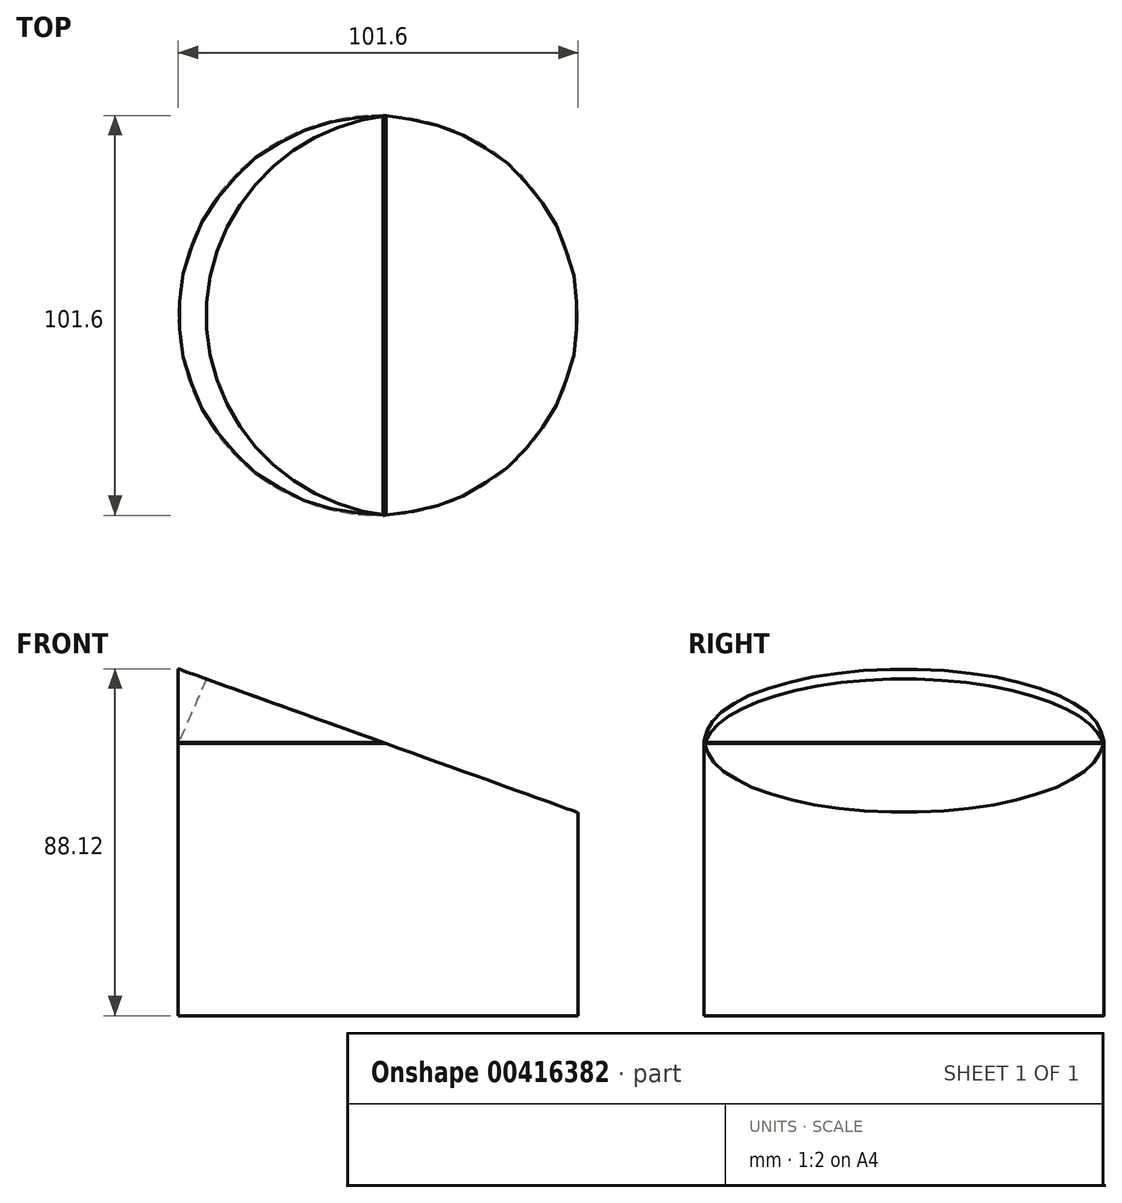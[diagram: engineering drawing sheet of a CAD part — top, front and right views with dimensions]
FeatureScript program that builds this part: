
annotation { "Feature Type Name" : "Feature", "Feature Type Description" : "" }
export const myFeature = defineFeature(function(context is Context, id is Id, definition is map)
    precondition{}
    {
        {
            var Q0;
            Q0=qCreatedBy(makeId("Front.planeOp"),FACE);
            var sketch = newSketch(context, id + "F0", { "sketchPlane" : qUnion([Q0])});
            skLineSegment(sketch, "E0", {"start": v(0, 0) * mm, "end": v(101.6, 0) * mm});
            skLineSegment(sketch, "E1", {"start": v(0, 0) * mm, "end": v(-101.6, 0) * mm});
            skFitSpline(sketch, "E2", {"points": [v(-101.6, 0) * mm, v(0, 152.4) * mm, v(101.6, 0) * mm], "startDerivative": vector(212.3, 35.26) * mm, "endDerivative": vector(256.16, -42) * mm});
            skLineSegment(sketch, "E3", {"start": v(0, 0) * mm, "end": v(0, 152.4) * mm});
            skSolve(sketch);
        }
        {
            var Q0;
            Q0=makeQuery(id+"F0.imprint","IMPRINT",FACE,{"disambiguationData":[TD([[makeQuery(id+"F0.imprint","IMPRINT",EDGE,{"derivedFrom":sQuery(id+"F0.wireOp",EDGE,"E0")}),1.0]])]});
            var Q1;
            Q1=sQuery(id+"F0.wireOp",EDGE,"E3");
            revolve(context, id + "F1", {"entities" : qUnion([Q0]), "axis" : qUnion([Q1]), "revolveType" : RevolveType.FULL});
        }
        {
            var Q0;
            Q0=qCreatedBy(makeId("Right.planeOp"),FACE);
            var sketch = newSketch(context, id + "F2", { "sketchPlane" : qUnion([Q0])});
            skLineSegment(sketch, "E4", {"start": v(0, 0) * mm, "end": v(0, 107.44) * mm});
            skSolve(sketch);
        }
        {
            var Q0;
            Q0=qCreatedBy(makeId("Front.planeOp"),FACE);
            var sketch = newSketch(context, id + "F3", { "sketchPlane" : qUnion([Q0])});
            skLineSegment(sketch, "E5", {"start": v(194.23, 0) * mm, "end": v(-165.07, 129.22) * mm});
            skPoint(sketch, "E6", {"position": v(0, 69.85) * mm});
            skLineSegment(sketch, "E7", {"start": v(-165.07, 129.22) * mm, "end": v(-130.7, 224.82) * mm});
            skLineSegment(sketch, "E8", {"start": v(194.23, 0) * mm, "end": v(228.61, 95.6) * mm});
            skLineSegment(sketch, "E9", {"start": v(-130.7, 224.82) * mm, "end": v(228.61, 95.6) * mm});
            skSolve(sketch);
        }
        {
            var Q0;
            Q0=qCreatedBy(makeId("Top.planeOp"),FACE);
            var sketch = newSketch(context, id + "F4", { "sketchPlane" : qUnion([Q0])});
            skCircle(sketch, "E10", {"center": v(0, 0) * mm, "radius": 50.8 * mm});
            skCircle(sketch, "E11", {"center": v(0, 0) * mm, "radius": 164.6 * mm});
            skSolve(sketch);
        }
        {
            var Q0;
            Q0 = qSketchRegion(id + "F4", true);
            extrude(context, id + "F5", {"entities" : qUnion([Q0]), "operationType" : NewBodyOperationType.REMOVE, "depth" : 228.6 * mm});
        }
        {
            var Q0;
            Q0 = qSketchRegion(id + "F3", true);
            extrude(context, id + "F6", {"entities" : qUnion([Q0]), "endBound" : BoundingType.SYMMETRIC, "depth" : 152.4 * mm});
        }
        {
            var Q0;
            Q0 = qSketchRegion(id + "F3", true);
            extrude(context, id + "F7", {"entities" : qUnion([Q0]), "operationType" : NewBodyOperationType.ADD, "endBound" : BoundingType.SYMMETRIC, "oppositeDirection" : true, "depth" : 152.4 * mm});
        }
        {
            var Q0;
            Q0=qCreatedBy(makeId("Top.planeOp"),FACE);
            cPlane(context, id + "F8", {"entities" : qUnion([Q0]), "cplaneType" : CPlaneType.OFFSET, "offset" : 88.9 * mm, "width" : 152.4 * mm, "height" : 152.4 * mm});
        }
        {
            var Q0;
            Q0=qCreatedBy(id+"F8.planeOp",FACE);
            var sketch = newSketch(context, id + "F9", { "sketchPlane" : qUnion([Q0])});
            skCircle(sketch, "E12", {"center": v(0, 0) * mm, "radius": 50.8 * mm});
            skSolve(sketch);
        }
        {
            var Q0;
            Q0=makeQuery(id+"F1.opRevolve","SWEPT_FACE",FACE,{"disambiguationData":[OSD([sQuery(id+"F0.wireOp",EDGE,"E0")])]});
            var Q1;
            Q1 = qSketchRegion(id + "F9", true);
            extrude(context, id + "F10", {"entities" : qUnion([Q0, Q1]), "depth" : 0.25 * mm});
        }
        {
            var Q0;
            Q0=makeQuery(id+"F10.opExtrude","SWEPT_BODY",BODY,{"disambiguationData":[OSD([sQuery(id+"F0.wireOp",EDGE,"E0")])]});
            deleteBodies(context, id + "F11", {"entities" : qUnion([Q0])});
        }
        {
            var Q0;
            Q0=qCreatedBy(makeId("Top.planeOp"),FACE);
            cPlane(context, id + "F12", {"entities" : qUnion([Q0]), "cplaneType" : CPlaneType.OFFSET, "offset" : 69.14 * mm, "width" : 152.4 * mm, "height" : 152.4 * mm});
        }
        {
            var Q0;
            Q0=qCreatedBy(id+"F12.planeOp",FACE);
            var sketch = newSketch(context, id + "F13", { "sketchPlane" : qUnion([Q0])});
            skCircle(sketch, "E13", {"center": v(0, 0) * mm, "radius": 50.8 * mm});
            skSolve(sketch);
        }
        {
            var Q0;
            Q0 = qSketchRegion(id + "F13", true);
            extrude(context, id + "F14", {"entities" : qUnion([Q0]), "depth" : 0.25 * mm, "offsetDistance" : 25.4 * mm});
        }
        {
            var Q0;
            Q0=qCreatedBy(id+"F12.planeOp",FACE);
            var sketch = newSketch(context, id + "F15", { "sketchPlane" : qUnion([Q0])});
            skCircle(sketch, "E14", {"center": v(0, 0) * mm, "radius": 50.8 * mm});
            skSolve(sketch);
        }
        {
            var Q0;
            Q0 = qSketchRegion(id + "F15", true);
            extrude(context, id + "F16", {"entities" : qUnion([Q0]), "depth" : 88.9 * mm, "offsetDistance" : 25.4 * mm});
        }
        {
            var Q0;
            Q0 = qSketchRegion(id + "F3", true);
            extrude(context, id + "F17", {"entities" : qUnion([Q0]), "operationType" : NewBodyOperationType.REMOVE, "endBound" : BoundingType.THROUGH_ALL, "oppositeDirection" : true, "depth" : 25.4 * mm, "offsetDistance" : 25.4 * mm, "hasSecondDirection" : true, "secondDirectionBound" : SecondDirectionBoundingType.THROUGH_ALL, "secondDirectionOppositeDirection" : false, "secondDirectionDepth" : 25.4 * mm});
        }
    });
